# Revit family: PRD_AR_MltFnctnDspnsrs_RODANPaperTowelSoapDispenserWasteBinCombination_RODX617_RODX617E
name_source: partatom
category: Specialty Equipment
revit_build: Autodesk Revit 2018 (Build: 20190510_1515(x64)
units: mm (PartAtom-declared; Revit-internal decimal feet)

## family parameters
Cut with Voids When Loaded = Yes
Host = Face
OmniClass Number = 23.40.20.21.17
OmniClass Title = Paper Towel Dispensers, Disposal Units
Part Type = Normal
Room Calculation Point = No
Round Connector Dimension = Use Diameter
Shared = No

## types (2) — shared parameters
AssetType = Fixed
Category = Pr_40_70_22_52, Multi-function dispensers
CombinationPart1 = Paper towel dispenser
CombinationPart2 = Soap dispenser
CombinationPart3 = Waste bin
Default Elevation = 800 mm  [stored 2.62467 ft]
DispenserMaterial = PRD_AR_StainlessSteel_SatinFinished
DurationUnit = year
Features = stainless steel, surface satin finished
FillingQuantity1 = 400
FillingQuantity1Uom = Pieces
FillingQuantity2 = 0.8
FillingQuantity2Uom = Liter
FillingQuantity3 = 23
FillingQuantity3Uom = Liter
Finish = satin finished
IfcExportAs = IfcFurnitureType
IfcExportType = USERDEFINED
IntegralAccessories = incl. stainless steel screws and dowels
IsBuiltIn = TRUE
Lock1 = Key-lock
Lock2 = Key-lock
Lock3 = Key-lock
MainColor = stainless steel
Manufacturer = KWC Group AG
ManufacturerName = KWC Group AG
ManufacturerURL = www.kwc.com
Material = stainless steel
MaterialCode = 1.4301
MaterialThickness = 0.80 mm
NBSDescription = Multi-function dispensers
NBSReference = 45-35-72/384
ProductInformation = https://pim.kwc.com
TypeOfConsumable1 = Paper towel
TypeOfConsumable2 = Liquid soap
TypeOfFixing = Screw
URL = www.kwc.com
Uniclass2015Code = Pr_40_70_22_52
Uniclass2015Title = Multi-function dispensers
Uniclass2015Version = Products v1.10
Version = 1
WarrantyDurationUnit = year

## per-type parameters (varying)
| type | BIMObjectName | Description | GrossWeight | ModelNumber | ModelOffset | Name | NetWeight | NominalDepth | NominalHeight | NominalWidth | Size | TypeOfMounting | VoidOffset |
| RODX617 | PRD_AR_MultiFunctionDispensers_RODANPaperTowelSoapDispenserWasteBinCombination_RODX617 | Waste bin, paper towel-, soap dispenser combination for wall mounting, stainless steel, surface satin finished, material thickness 0.8 mm, cylinder lock with KWC standard key, paper towel dispenser with loading capacity 300 - 400 pcs. of paper depending on convolution, suitable for liquid soaps and lotions, 0.8 liter soap tank, push lever, waste bin with approx. 23 liter capacity, inclusive stainless steel screws and dowels. | 20.10 kg | 2000101219 | 114 mm  [stored 0.374016 ft] | Paper Towel Soap Dispenser Waste Bin Combination RODX617 | 16.75 kg | 173 mm  [stored 0.567585 ft] | 1148 mm  [stored 3.7664 ft] | 413 mm  [stored 1.35499 ft] | 413 x 1148 x 173 mm | Wall mounting | 150 mm |
| RODX617E | PRD_AR_MultiFunctionDispensers_RODANPaperTowelSoapDispenserWasteBinCombination_RODX617E | Paper towel-, soap dispenser and waste bin combination for recessed mounting, stainless steel, surface satin finished, material thickness 0.8 mm, cylinder lock with KWC standard key, paper towel dispenser with loading capacity 300 - 400 pcs. of paper depending on convolution, suitable for liquid soaps and lotions, 0.8 liter soap tank, push lever, waste bin with approx. 23 liter capacity, includes stainless steel screws and dowels. | 14.31 kg | 2000101220 | 0 mm  [stored 0 ft] | Paper Towel Soap Dispenser Waste Bin Combination RODX617E | 12.31 kg | 169 mm  [stored 0.554462 ft] | 1145 mm  [stored 3.75656 ft] | 408 mm | 408 x 1145 x 169 mm | Recessed mounting | 36 mm  [stored 0.11811 ft] |

note: column(s) folded — value = type name in every type: Model, ModelReference, Type

note: [stored X ft] marks values corroborated as IEEE doubles in the binary element streams (Revit-internal decimal feet)

## geometry (parser evidence)
native form markers: Sweep x1
no freeform markers — native parametric forms only
